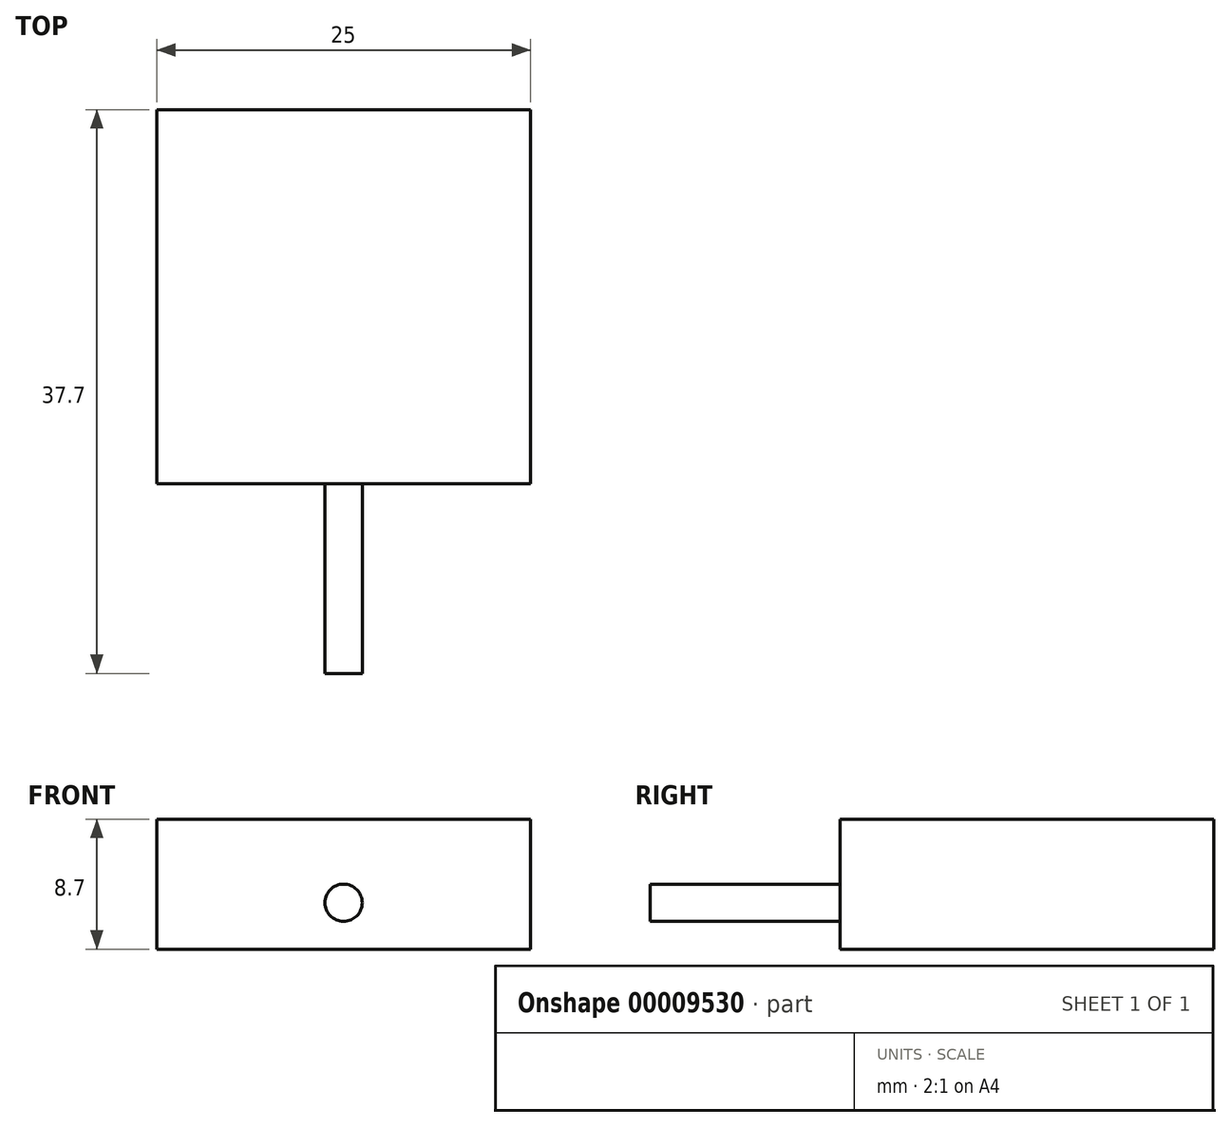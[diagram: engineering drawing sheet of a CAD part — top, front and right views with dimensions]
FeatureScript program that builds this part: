
annotation { "Feature Type Name" : "Feature", "Feature Type Description" : "" }
export const myFeature = defineFeature(function(context is Context, id is Id, definition is map)
    precondition{}
    {
        {
            var Q0;
            Q0=qCreatedBy(makeId("Top.planeOp"),FACE);
            var sketch = newSketch(context, id + "F0", { "sketchPlane" : qUnion([Q0])});
            skLineSegment(sketch, "E0.rect.bottom", {"start": v(12.5, 12.5) * mm, "end": v(-12.5, 12.5) * mm});
            skLineSegment(sketch, "E0.rect.top", {"start": v(12.5, -12.5) * mm, "end": v(-12.5, -12.5) * mm});
            skLineSegment(sketch, "E0.rect.left", {"start": v(12.5, 12.5) * mm, "end": v(12.5, -12.5) * mm});
            skLineSegment(sketch, "E0.rect.right", {"start": v(-12.5, 12.5) * mm, "end": v(-12.5, -12.5) * mm});
            skPoint(sketch, "E0.rect.middle", {"position": v(0, 0) * mm});
            skSolve(sketch);
        }
        {
            var Q0;
            Q0=makeQuery(id+"F0.imprint","IMPRINT",FACE,{"disambiguationData":[TD([[makeQuery(id+"F0.imprint","IMPRINT",EDGE,{"derivedFrom":sQuery(id+"F0.wireOp",EDGE,"E0.rect.bottom")}),1.0]])]});
            extrude(context, id + "F1", {"entities" : qUnion([Q0]), "depth" : 8.7 * mm});
        }
        {
            var Q0;
            Q0=makeQuery(id+"F1.opExtrude","SWEPT_FACE",FACE,{"disambiguationData":[OSD([sQuery(id+"F0.wireOp",EDGE,"E0.rect.top")])]});
            var sketch = newSketch(context, id + "F2", { "sketchPlane" : qUnion([Q0])});
            skLineSegment(sketch, "E1", {"start": v(12.5, 4.35) * mm, "end": v(-12.5, 4.35) * mm, "construction": true});
            skPoint(sketch, "E2", {"position": v(0, 4.35) * mm});
            skCircle(sketch, "E3", {"center": v(0, 3.1) * mm, "radius": 1.25 * mm});
            skSolve(sketch);
        }
        {
            var Q0;
            Q0=makeQuery(id+"F2.imprint","IMPRINT",FACE,{"disambiguationData":[TD([[makeQuery(id+"F2.imprint","IMPRINT",EDGE,{"derivedFrom":sQuery(id+"F2.wireOp",EDGE,"E3")}),1.0]])]});
            var Q1;
            Q1=sQuery(id+"F2.wireOp",EDGE,"E3");
            extrude(context, id + "F3", {"entities" : qUnion([Q0]), "operationType" : NewBodyOperationType.ADD, "surfaceEntities" : qUnion([Q1]), "depth" : 12.7 * mm});
        }
        {
            var Q0;
            Q0=makeQuery(id+"F1.opExtrude","SWEPT_BODY",BODY,{"disambiguationData":[OSD([sQuery(id+"F0.wireOp",EDGE,"E0.rect.bottom"),sQuery(id+"F0.wireOp",EDGE,"E0.rect.top"),sQuery(id+"F0.wireOp",EDGE,"E0.rect.left"),sQuery(id+"F0.wireOp",EDGE,"E0.rect.right")])]});
            transform(context, id + "F4", {"entities" : qUnion([Q0]), "transformType" : TransformType.TRANSLATION_3D, "dx" : 0 * mm, "dy" : 0 * mm, "dz" : 0 * mm, "makeCopy" : true});
        }
    });
